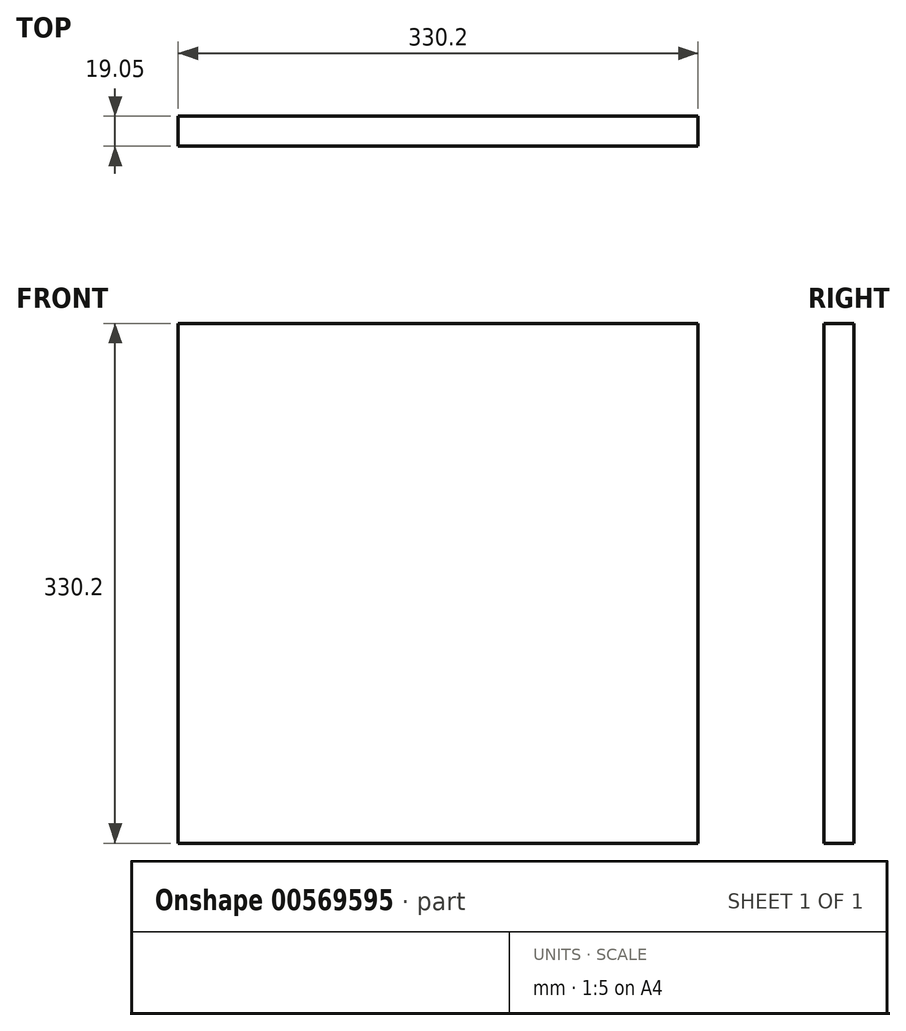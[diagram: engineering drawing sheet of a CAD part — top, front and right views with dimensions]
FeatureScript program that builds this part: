
annotation { "Feature Type Name" : "Feature", "Feature Type Description" : "" }
export const myFeature = defineFeature(function(context is Context, id is Id, definition is map)
    precondition{}
    {
        {
            var Q0;
            Q0=qCreatedBy(makeId("Front.planeOp"),FACE);
            var sketch = newSketch(context, id + "F0", { "sketchPlane" : qUnion([Q0])});
            skLineSegment(sketch, "E0.bottom", {"start": v(165.1, -165.1) * mm, "end": v(-165.1, -165.1) * mm});
            skLineSegment(sketch, "E0.top", {"start": v(165.1, 165.1) * mm, "end": v(-165.1, 165.1) * mm});
            skLineSegment(sketch, "E0.left", {"start": v(165.1, -165.1) * mm, "end": v(165.1, 165.1) * mm});
            skLineSegment(sketch, "E0.right", {"start": v(-165.1, -165.1) * mm, "end": v(-165.1, 165.1) * mm});
            skPoint(sketch, "E0.middle", {"position": v(0, 0) * mm});
            skSolve(sketch);
        }
        {
            var Q0;
            Q0 = qSketchRegion(id + "F0", true);
            extrude(context, id + "F1", {"entities" : qUnion([Q0]), "depth" : 19.05 * mm, "offsetDistance" : 25.4 * mm});
        }
    });
